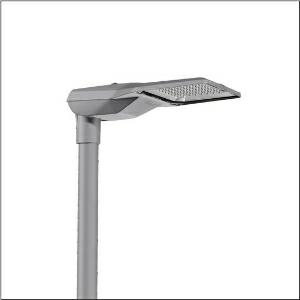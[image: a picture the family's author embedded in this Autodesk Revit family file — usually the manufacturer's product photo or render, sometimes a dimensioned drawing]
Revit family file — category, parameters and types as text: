
# Revit family: streetlight_sl_21_midi___pc-l_5xe3f33s08mb_4952
name_source: partatom
category: Lighting Fixtures
units: mm (PartAtom-declared; Revit-internal decimal feet)

## family parameters
Cut with Voids When Loaded = No
Host = Face
Light Source = No
Part Type = Normal
Room Calculation Point = No
Round Connector Dimension = Use Diameter
Shared = No

## types (1)
- --- (1 x LED, 17390 lm, 136 W, 3000K)
    Apparent Load = 136 VA
    CIE Flux Codes = 38 78 98 100 100
    Color Rendering = 70
    Color Temperature = 3000K
    Default Elevation = 1800 mm
    Description = Streetlight SL 21 midi, mast luminaire, primary light control with lens, of PMMA, primary optical cover: cover, of toughened safety glass, transparent, light distribution: PC-L, light emission: direct distribution, primary light characteristic: asymmetric, left, installation type: side-entry, post-top, LED, High Power LED, rated luminous flux: 17.390lm, luminous efficacy: 128lm/W, light colour: 730, colour temperature: 3000K, control gear: D4i, control: overheat protection, constant luminous flux control, time-dependent luminous flux control, flexible luminous flux parameterisation, pre-setting: logarithmic dimming characteristic, mains connection: 230..240V, AC, 50/60Hz, start of lifetime: 136W, end of service life: 142W, reduction: 61W, luminaire housing, of diecast aluminium, powder-coated, Siteco® metallic grey (DB 702S), corrosivity category C5 mid according to DIN EN ISO 12944, please order mast flange separately, inclination adjustable: 0°, 5°, 10°, 15°, sealing non-destructively replaceable, multi-level sealing system, length: 644mm, width: 335mm, height: 110mm, mast flange for spigot size: 42mm (side-entry): 5XC10008XM4, 60/48mm (side-entry/post-top): 5XC10108XM2, 76/60mm (side-entry/post-top): 5XC10108XM1, mounting height: 4..8m, Smart Interface above, protection rating (complete): IP66, insulation class (complete): insulation class II (safety insulation), certification: CE, ENEC, ENEC+, VDE, impact resistance: IK10, permissible operating ambient temperature for outdoor applications: -40..+50°C, standard-compliant lighting for roads and squares, packaging unit: 1 piece

Light Distribution: PC-L
    Height = 111 mm
    Lamp = 1 x LED
    Lamp Light Flux = 17390 lm
    Lamp Power = 136 W
    Lamp count = 1
    Length = 644 mm
    Luminous efficacy = 128 lm/W
    Manufacturer = Siteco
    ModVariant = No
    Model = 5XE3F33S08MB
    Number of Poles = 1
    OnlyDefault = Yes
    Power Factor = 1
    Product Name = Streetlight SL 21 midi | PC-L
    Product group = mast luminaire | pylon top
    ProductGroupID = 6100
    Protection Class = Protection class II
    Protection Degree = IP 66
    RLX_Detail_Level = 1
    RLX_Emergency_Light_Flux = 0 lm
    RLX_Emergency_Type = 0
    RLX_Emergency_Type_DB = No
    RlxData = <blob elided: 29497 chars, md5=98cfc87a>
    Socket = socket
    Standby Power = 0 W
    System Light Flux = 17390 lm
    System Power = 136 W
    Type Comments = factory setting: luminous flux: 100 % | dim-lin: 254 | 695 mA
    Type Image = l_1004302.jpg
    URL = http://relux.com
    VarID = @adj_085915
    Voltage = 0 V
    Weight = 0.00 kg
    Width = 336 mm

## geometry (parser evidence)
native form markers: Blend x4, Sweep x11
no freeform markers — native parametric forms only
